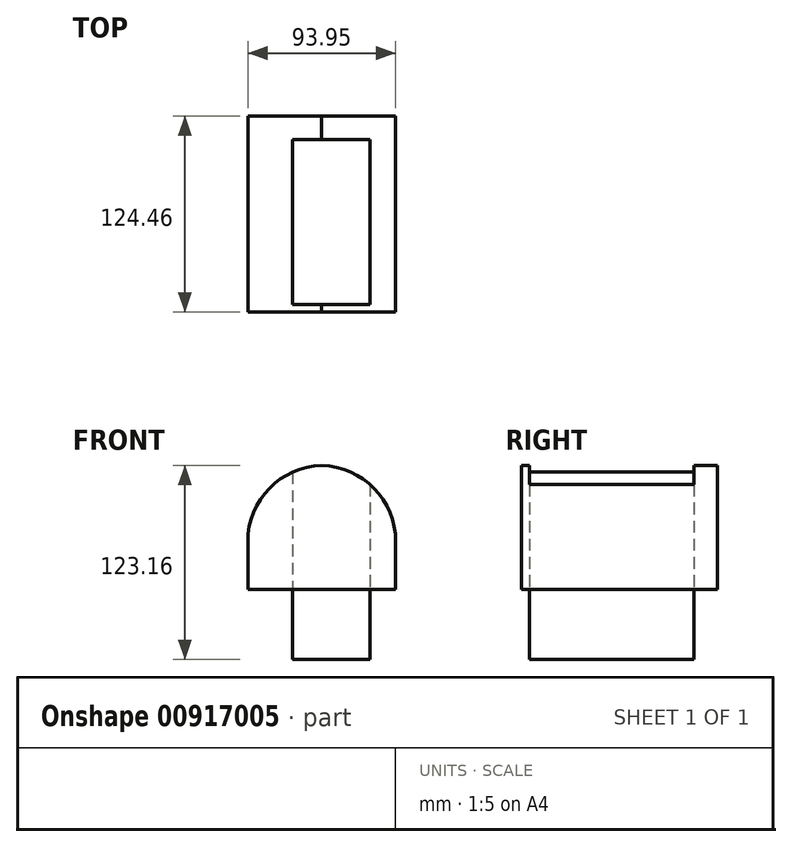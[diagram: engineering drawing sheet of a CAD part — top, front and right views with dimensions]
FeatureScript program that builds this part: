
annotation { "Feature Type Name" : "Feature", "Feature Type Description" : "" }
export const myFeature = defineFeature(function(context is Context, id is Id, definition is map)
    precondition{}
    {
        {
            var Q0;
            Q0=qCreatedBy(makeId("Front.planeOp"),FACE);
            var sketch = newSketch(context, id + "F0", { "sketchPlane" : qUnion([Q0])});
            skLineSegment(sketch, "E0.bottom", {"start": v(-89.01, 9.87) * mm, "end": v(-138.15, 9.87) * mm});
            skLineSegment(sketch, "E0.top", {"start": v(-89.01, 54.3) * mm, "end": v(-138.15, 54.3) * mm});
            skLineSegment(sketch, "E0.left", {"start": v(-89.01, 9.87) * mm, "end": v(-89.01, 54.3) * mm});
            skLineSegment(sketch, "E0.right", {"start": v(-138.15, 9.87) * mm, "end": v(-138.15, 54.3) * mm});
            skPoint(sketch, "E0.middle", {"position": v(-113.58, 32.09) * mm});
            skSolve(sketch);
        }
        {
            var Q0;
            Q0=makeQuery(id+"F0.imprint","IMPRINT",FACE,{"disambiguationData":[TD([[makeQuery(id+"F0.imprint","IMPRINT",EDGE,{"derivedFrom":sQuery(id+"F0.wireOp",EDGE,"E0.bottom")}),-1.0]])]});
            extrude(context, id + "F1", {"entities" : qUnion([Q0]), "depth" : 104.65 * mm, "offsetDistance" : 25.4 * mm});
        }
        {
            var Q0;
            Q0=makeQuery(id+"F1.opExtrude","SWEPT_FACE",FACE,{"disambiguationData":[OSD([sQuery(id+"F0.wireOp",EDGE,"E0.top")])]});
            var sketch = newSketch(context, id + "F2", { "sketchPlane" : qUnion([Q0])});
            skLineSegment(sketch, "E1.bottom", {"start": v(-166.64, 14.95) * mm, "end": v(-72.69, 14.95) * mm});
            skLineSegment(sketch, "E1.top", {"start": v(-166.64, -109.5) * mm, "end": v(-72.69, -109.5) * mm});
            skLineSegment(sketch, "E1.left", {"start": v(-166.64, 14.95) * mm, "end": v(-166.64, -109.5) * mm});
            skLineSegment(sketch, "E1.right", {"start": v(-72.69, 14.95) * mm, "end": v(-72.69, -109.5) * mm});
            skPoint(sketch, "E1.middle", {"position": v(-119.67, -47.28) * mm});
            skSolve(sketch);
        }
        {
            var Q0;
            Q0=makeQuery(id+"F2.imprint","IMPRINT",FACE,{"disambiguationData":[TD([[makeQuery(id+"F2.imprint","IMPRINT",EDGE,{"derivedFrom":sQuery(id+"F2.wireOp",EDGE,"E1.bottom")}),-1.0]])]});
            extrude(context, id + "F3", {"entities" : qUnion([Q0]), "depth" : 78.74 * mm, "offsetDistance" : 25.4 * mm});
        }
        {
            var Q0;
            Q0=makeQuery(id+"F3.opExtrude","CAP_EDGE",EDGE,{"disambiguationData":[OSD([sQuery(id+"F2.wireOp",EDGE,"E1.right")])],"isStart":false});
            var Q1;
            Q1=makeQuery(id+"F3.opExtrude","CAP_EDGE",EDGE,{"disambiguationData":[OSD([sQuery(id+"F2.wireOp",EDGE,"E1.left")])],"isStart":false});
            fillet(context, id + "F4", {"entities" : qUnion([Q0, Q1]), "radius" : 48.26 * mm, "tangentPropagation" : true, "allowEdgeOverflow" : false});
        }
    });
